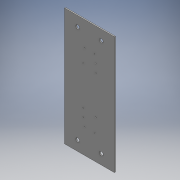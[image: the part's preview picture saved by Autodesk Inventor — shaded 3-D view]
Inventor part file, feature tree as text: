
AUTODESK INVENTOR PART (.ipt)
format: ipt  version: 2016 (Build 200138000, 138)  size: 152,064 bytes
history: native  units: mm
features: extrude x2, sketch x2, other x1
ambient origin geometry x8: Origin, YZ Plane, XZ Plane, XY Plane, X Axis, Y Axis, Z Axis, Center Point
bodies: Body1 (feature_tree)
feature tree (5):
  other  "ソリッド1"
  extrude  "押し出し1"  Depth=110.0mm
  extrude  "押し出し7"  Depth=260.0mm
  sketch  "スケッチ1"
  sketch  "スケッチ2"
